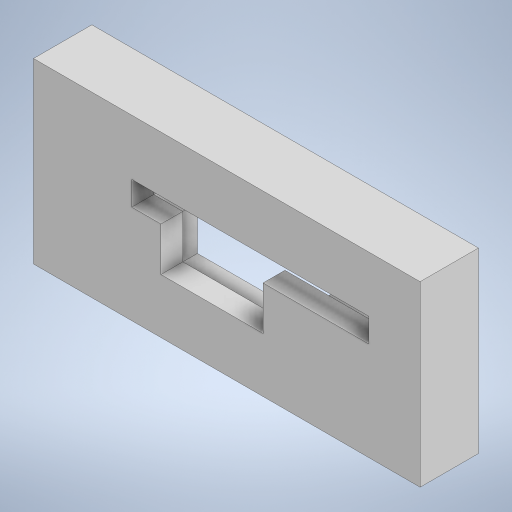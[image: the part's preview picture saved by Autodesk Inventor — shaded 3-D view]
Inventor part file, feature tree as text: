
AUTODESK INVENTOR PART (.ipt)
format: ipt  version: 2023 (Build 270158000, 158)  size: 633,344 bytes
history: native  units: in
note: dims shown in document units (in); Inventor stores cm internally (conversion verified against a paired STEP export)
features: extrude x17, sketch x15, fillet x2
ambient origin geometry x8: Origin, YZ Plane, XZ Plane, XY Plane, X Axis, Y Axis, Z Axis, Center Point
bodies: Solid1 (feature_tree)
feature tree (34):
  extrude  "Extrusion1"  Depth=7.0in
  extrude  "Extrusion2"  Depth=0.2in
  fillet  "Fillet1"  Radius=1.4in
  extrude  "Extrusion3"  Depth=0.125in
  extrude  "Extrusion4"  Depth=2.2875in
  extrude  "Extrusion5"  Depth=0.5437in
  sketch  "Sketch6"  dims[d13=0.75in d14=1.4in d15=0.0in]
  extrude  "Extrusion6"  Depth=1.4in TaperAngle=0.0deg
  extrude  "Extrusion9"  Depth=0.1in
  extrude  "Extrusion10"  Depth=0.1in
  extrude  "Extrusion11"  Depth=0.35in
  extrude  "Extrusion12"  Depth=0.15in
  extrude  "Extrusion13"  Depth=0.7in
  extrude  "Extrusion14"  Depth=0.1in
  extrude  "Extrusion15"  Depth=0.615in
  extrude  "Extrusion16"  Depth=1.1in
  fillet  "Fillet2"  Radius=0.21in
  extrude  "Extrusion17"  Depth=0.5in
  extrude  "Extrusion18"  Depth=0.5in
  extrude  "Extrusion19"  Depth=0.3075in
  sketch  "Sketch1"  dims[d0=7.0in d1=4.5in]
  sketch  "Sketch2"  dims[d2=1.5in d3=0.0in d4=0.2in d5=1.4in d6=0.0in]
  sketch  "Sketch3"  dims[d7=0.125in d8=0.25in]
  sketch  "Sketch4"  dims[d9=0.25in d10=2.2875in]
  sketch  "Sketch5"  dims[d11=3.4125in d12=0.5437in]
  sketch  "Sketch8"  dims[d16=0.1in d17=0.14in]
  sketch  "Sketch9"  dims[d18=0.1in d19=0.275in]
  sketch  "Sketch10"  dims[d20=0.35in d21=0.25in]
  sketch  "Sketch11"  dims[d22=0.15in d23=0.15in]
  sketch  "Sketch12"  dims[d24=0.25in d25=0.7in]
  sketch  "Sketch13"  dims[d26=0.1in d27=0.1in]
  sketch  "Sketch14"  dims[d28=0.25in d29=0.615in]
  sketch  "Sketch15"  dims[d30=0.25in d31=1.1in d32=0.21in]
  sketch  "Sketch16"  dims[d33=0.3075in d34=0.5575in d35=1.65in d36=0.3075in d37=0.21in d38=0.5575in d39=2.1in d40=0.1in d41=0.1in d42=0.3in d43=0.1in d44=0.25in d45=0.615in d46=2.4in d47=0.11in d48=2.51in d49=0.5575in d50=0.1in d51=0.615in d52=0.175in d53=0.175in d54=0.1in d55=0.1in d56=0.25in d57=3.15in d58=0.1in d59=0.515in d60=0.05in d61=0.0in d62=0.1562in d63=0.1562in d64=0.2188in d65=0.2188in d66=0.2188in d67=0.2188in d68=0.2188in d69=0.2188in d70=0.625in d71=0.625in d72=0.625in d73=0.625in d74=0.8906in d76=2.25in d77=0.3in d78=0.3in d79=0.3in d80=0.3in d81=0.3in d82=0.625in d83=0.625in d84=0.625in d85=0.625in d86=1.0in d87=3.1in d88=3.1in d89=3.1in d90=3.1in d91=3.1in d92=1.0in d93=0.0in d97=0.4in d98=0.4in d99=0.4in d100=0.4in d101=0.4in d102=0.05in d103=0.0in d119=0.075in d120=0.075in d121=0.075in d122=0.075in d123=0.075in d124=0.0688in d125=0.0in d126=0.25in d127=0.275in d128=0.25in d129=0.25in d130=0.25in d131=2.1in d132=0.125in d133=0.0625in d134=0.05in d135=0.0in d136=0.6in d137=3.35in d139=0.3in d140=0.3155in d141=0.3157in d142=0.0375in d143=0.0in d144=2.0in d145=0.8125in d146=0.0825in d147=0.35in d148=0.15in d149=0.1in d150=0.7in d151=0.2in d152=0.0in d153=0.075in d154=0.125in d155=0.0in d156=0.3in d157=2.5in d158=0.5in d159=0.25in d160=0.0in d161=0.5in d162=0.081in d163=0.0in d164=0.45in d165=0.6in d166=0.2in d167=0.2in d168=0.2in d169=0.075in d170=0.075in d171=0.075in d172=0.075in d173=0.2in d174=0.2in d175=0.2in d176=0.2in d177=0.075in d178=0.0in d179=0.125in d180=0.0375in d181=0.0375in d182=2.0in d183=0.5in d184=0.0in d185=0.0in d187=2.8in d188=5.0in d189=0.0in d190=5.0in d191=0.0in]
